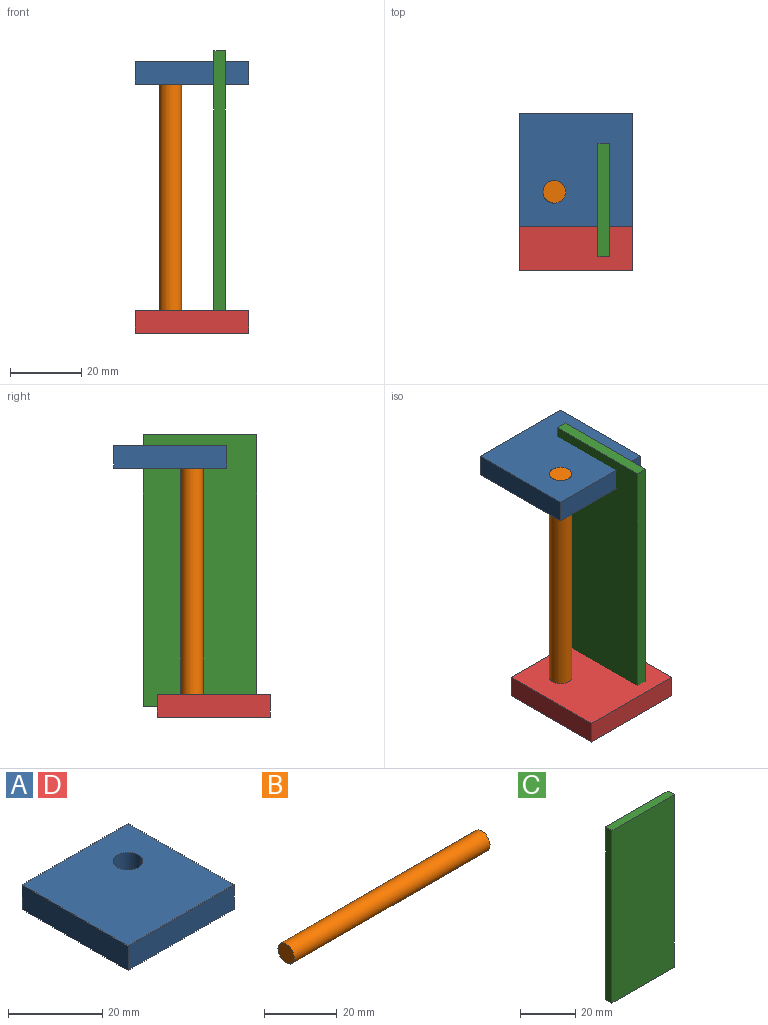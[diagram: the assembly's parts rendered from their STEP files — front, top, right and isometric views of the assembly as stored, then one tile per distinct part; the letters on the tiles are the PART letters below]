
ASSEMBLY  parts=4 mates=4
PART A: 7 faces, bbox 31.8x31.8x6.4 mm
  f0: plane 31.75x6.35mm, normal (0,1,0), area 201.6mm2, adj f1,f3,f4,f5
  f1: plane 31.75x6.35mm, normal (-1,0,0), area 201.6mm2, adj f0,f2,f4,f5
  f2: plane 31.75x6.35mm, normal (0,-1,0), area 201.6mm2, adj f1,f3,f4,f5
  f3: plane 31.75x6.35mm, normal (1,0,0), area 201.6mm2, adj f0,f2,f4,f5
  f4: plane 31.75x31.75mm, normal (0,0,1), area 976.4mm2, adj f0,f1,f2,f3,f6
  f5: plane 31.75x31.75mm, normal (0,0,-1), area 976.4mm2, adj f0,f1,f2,f3,f6
  f6: cylinder r=3.17mm len=6.35mm, axis (0,0,-1), area 126.7mm2, adj f4,f5
PART B: 3 faces, bbox 76.2x6.4x6.4 mm
  f0: cylinder r=3.17mm len=76.2mm, axis (-1,0,0), area 1520.1mm2, adj f1,f2
  f1: plane 6.35x6.35mm, normal (1,0,0), area 31.7mm2, adj f0
  f2: plane 6.35x6.35mm, normal (-1,0,0), area 31.7mm2, adj f0
PART C: 6 faces, bbox 31.8x3.2x76.2 mm
  f0: plane 76.2x3.18mm, normal (1,0,0), area 241.9mm2, adj f1,f3,f4,f5
  f1: plane 31.75x3.18mm, normal (0,0,1), area 100.8mm2, adj f0,f2,f4,f5
  f2: plane 76.2x3.18mm, normal (-1,0,0), area 241.9mm2, adj f1,f3,f4,f5
  f3: plane 31.75x3.18mm, normal (0,0,-1), area 100.8mm2, adj f0,f2,f4,f5
  f4: plane 76.2x31.75mm, normal (0,-1,0), area 2419.3mm2, adj f0,f1,f2,f3
  f5: plane 76.2x31.75mm, normal (0,1,0), area 2419.3mm2, adj f0,f1,f2,f3
PART D: same geometry as A
PLACE A rot(axis=(0,0,-1),180deg) t=(138.05,71.1,136.75)mm
PLACE B rot(axis=(-0.71,0,0.71),180deg) t=(102.66,52.22,143.1)mm
PLACE C rot(axis=(0,0,1),90deg) t=(128.34,52.04,42.49)mm
PLACE D rot(axis=(0,0,1),90deg) t=(106.3,58.91,66.9)mm
MATE parallel C.f5 <-> D.f2  axis (-1,0,0) through (128.34,78.64,107.98)mm
MATE parallel C.f1 <-> A.f4  axis (0,0,1) through (128.34,78.64,146.08)mm
MATE planar A.f4 <-> B.f0  axis (0,0,1) through (122.38,87.18,143.1)mm
MATE planar D.f5 <-> B.f0  axis (0,0,-1) through (122.38,74.59,66.9)mm
